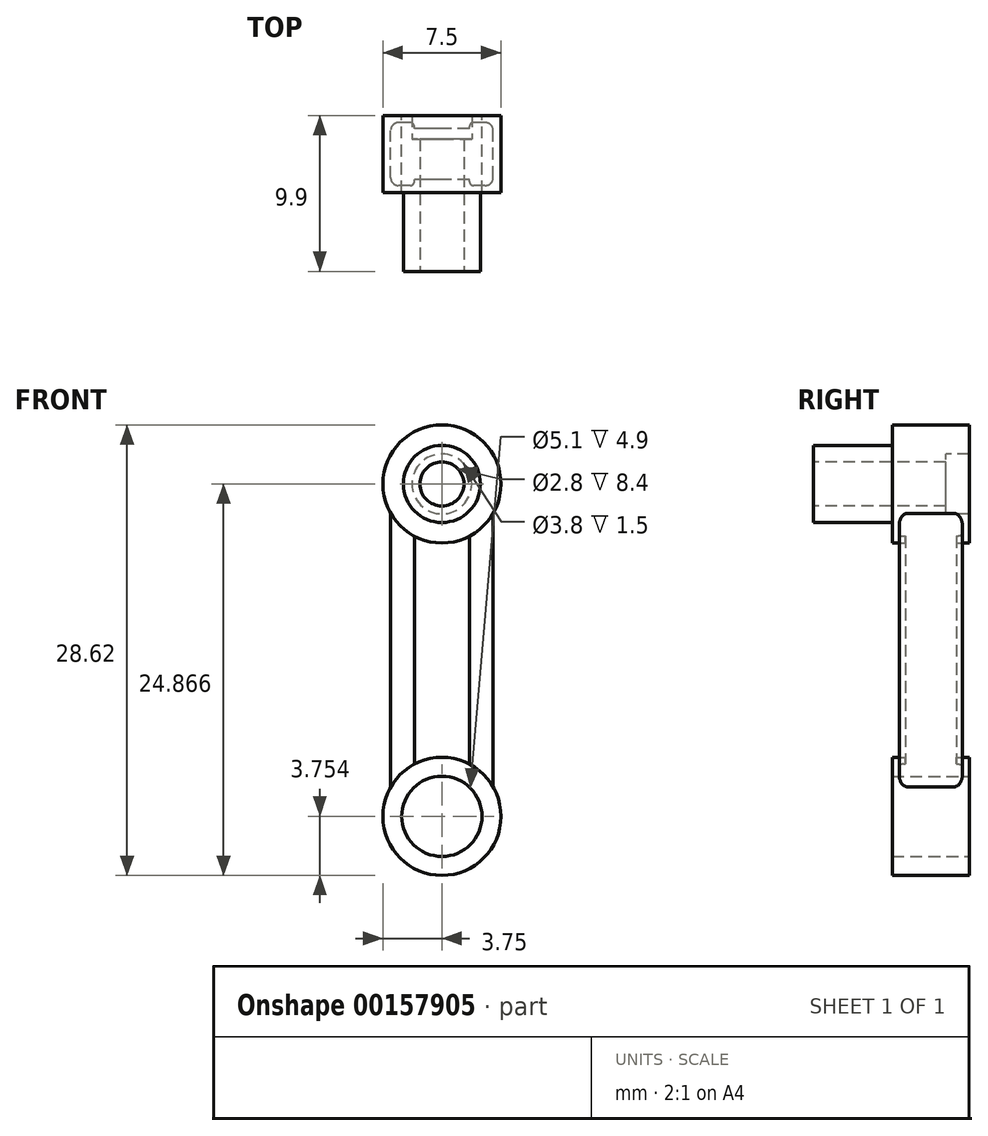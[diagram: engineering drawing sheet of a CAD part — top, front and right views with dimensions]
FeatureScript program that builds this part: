
annotation { "Feature Type Name" : "Feature", "Feature Type Description" : "" }
export const myFeature = defineFeature(function(context is Context, id is Id, definition is map)
    precondition{}
    {
        {
            var Q0;
            Q0=qCreatedBy(makeId("Front.planeOp"),FACE);
            var sketch = newSketch(context, id + "F0", { "sketchPlane" : qUnion([Q0])});
            skCircle(sketch, "E0", {"center": v(0, 10.56) * mm, "radius": 2.45 * mm});
            skCircle(sketch, "E1", {"center": v(0, -10.56) * mm, "radius": 2.55 * mm});
            skCircle(sketch, "E2", {"center": v(0, -10.56) * mm, "radius": 3.75 * mm});
            skCircle(sketch, "E3", {"center": v(0, 10.56) * mm, "radius": 3.75 * mm});
            skSolve(sketch);
        }
        {
            var Q0;
            Q0 = qSketchRegion(id + "F0", true);
            var Q1;
            Q1=makeQuery(id+"F0.imprint","IMPRINT",FACE,{"disambiguationData":[TD([[makeQuery(id+"F0.imprint","IMPRINT",EDGE,{"derivedFrom":sQuery(id+"F0.wireOp",EDGE,"E0")}),1.0]])]});
            extrude(context, id + "F1", {"entities" : qUnion([Q0, Q1]), "depth" : 4.9 * mm});
        }
        {
            var Q0;
            Q0=qCreatedBy(makeId("Top.planeOp"),FACE);
            var sketch = newSketch(context, id + "F2", { "sketchPlane" : qUnion([Q0])});
            skLineSegment(sketch, "E4.bottom", {"start": v(-2.75, -0.45) * mm, "end": v(-2, -0.45) * mm});
            skLineSegment(sketch, "E4.top", {"start": v(-2.75, -4.45) * mm, "end": v(-2, -4.45) * mm});
            skLineSegment(sketch, "E4.left", {"start": v(-3.25, -0.95) * mm, "end": v(-3.25, -3.95) * mm});
            skLineSegment(sketch, "E4.right", {"start": v(3.25, -0.95) * mm, "end": v(3.25, -3.95) * mm});
            skLineSegment(sketch, "E5.bottom", {"start": v(-1.75, -0.82) * mm, "end": v(1.75, -0.82) * mm});
            skLineSegment(sketch, "E5.top", {"start": v(-1.75, -4.08) * mm, "end": v(1.75, -4.08) * mm});
            skLineSegment(sketch, "E6", {"start": v(1.75, -4.08) * mm, "end": v(1.75, -4.2) * mm});
            skLineSegment(sketch, "E7", {"start": v(-1.75, -4.08) * mm, "end": v(-1.75, -4.2) * mm});
            skLineSegment(sketch, "E8", {"start": v(-1.75, -0.82) * mm, "end": v(-1.75, -0.7) * mm});
            skLineSegment(sketch, "E9", {"start": v(1.75, -0.82) * mm, "end": v(1.75, -0.7) * mm});
            skLineSegment(sketch, "E10.trimOffspring", {"start": v(2, -0.45) * mm, "end": v(2.75, -0.45) * mm});
            skLineSegment(sketch, "E11.trimOffspring", {"start": v(2, -4.45) * mm, "end": v(2.75, -4.45) * mm});
            skPoint(sketch, "E12.visualSharp", {"position": v(-1.75, -0.45) * mm});
            skArc(sketch, "E12.filletArc", {"start": v(-1.75, -0.7) * mm, "mid": v(-1.82, -0.52) * mm, "end": v(-2, -0.45) * mm});
            skPoint(sketch, "E13.visualSharp", {"position": v(1.75, -0.45) * mm});
            skArc(sketch, "E13.filletArc", {"start": v(2, -0.45) * mm, "mid": v(1.82, -0.52) * mm, "end": v(1.75, -0.7) * mm});
            skPoint(sketch, "E14.visualSharp", {"position": v(1.75, -4.45) * mm});
            skArc(sketch, "E14.filletArc", {"start": v(1.75, -4.2) * mm, "mid": v(1.82, -4.38) * mm, "end": v(2, -4.45) * mm});
            skPoint(sketch, "E15.visualSharp", {"position": v(-1.75, -4.45) * mm});
            skArc(sketch, "E15.filletArc", {"start": v(-2, -4.45) * mm, "mid": v(-1.82, -4.38) * mm, "end": v(-1.75, -4.2) * mm});
            skPoint(sketch, "E16.visualSharp", {"position": v(3.25, -4.45) * mm});
            skArc(sketch, "E16.filletArc", {"start": v(2.75, -4.45) * mm, "mid": v(3.1, -4.3) * mm, "end": v(3.25, -3.95) * mm});
            skPoint(sketch, "E17.visualSharp", {"position": v(3.25, -0.45) * mm});
            skArc(sketch, "E17.filletArc", {"start": v(3.25, -0.95) * mm, "mid": v(3.1, -0.6) * mm, "end": v(2.75, -0.45) * mm});
            skPoint(sketch, "E18.visualSharp", {"position": v(-3.25, -0.45) * mm});
            skArc(sketch, "E18.filletArc", {"start": v(-2.75, -0.45) * mm, "mid": v(-3.1, -0.6) * mm, "end": v(-3.25, -0.95) * mm});
            skPoint(sketch, "E19.visualSharp", {"position": v(-3.25, -4.45) * mm});
            skArc(sketch, "E19.filletArc", {"start": v(-3.25, -3.95) * mm, "mid": v(-3.1, -4.3) * mm, "end": v(-2.75, -4.45) * mm});
            skSolve(sketch);
        }
        {
            var Q0;
            Q0 = qSketchRegion(id + "F2", true);
            var Q1;
            Q1=makeQuery(id+"F1.opExtrude","SWEPT_FACE",FACE,{"disambiguationData":[OSD([sQuery(id+"F0.wireOp",EDGE,"E3")])]});
            extrude(context, id + "F3", {"entities" : qUnion([Q0]), "operationType" : NewBodyOperationType.ADD, "endBound" : BoundingType.UP_TO_SURFACE, "endBoundEntityFace" : qUnion([Q1]), "depth" : 25 * mm});
        }
        {
            var Q0;
            Q0=makeQuery(id+"F3.opExtrude","CAP_FACE",FACE,{"disambiguationData":[OSD([sQuery(id+"F2.wireOp",EDGE,"E4.bottom"),sQuery(id+"F2.wireOp",EDGE,"E4.top"),sQuery(id+"F2.wireOp",EDGE,"E4.left"),sQuery(id+"F2.wireOp",EDGE,"E4.right"),sQuery(id+"F2.wireOp",EDGE,"E5.bottom"),sQuery(id+"F2.wireOp",EDGE,"E5.top"),sQuery(id+"F2.wireOp",EDGE,"E6"),sQuery(id+"F2.wireOp",EDGE,"E7"),sQuery(id+"F2.wireOp",EDGE,"E8"),sQuery(id+"F2.wireOp",EDGE,"E9"),sQuery(id+"F2.wireOp",EDGE,"E10.trimOffspring"),sQuery(id+"F2.wireOp",EDGE,"E11.trimOffspring"),sQuery(id+"F2.wireOp",EDGE,"E12.filletArc"),sQuery(id+"F2.wireOp",EDGE,"E13.filletArc"),sQuery(id+"F2.wireOp",EDGE,"E14.filletArc"),sQuery(id+"F2.wireOp",EDGE,"E15.filletArc"),sQuery(id+"F2.wireOp",EDGE,"E16.filletArc"),sQuery(id+"F2.wireOp",EDGE,"E17.filletArc"),sQuery(id+"F2.wireOp",EDGE,"E18.filletArc"),sQuery(id+"F2.wireOp",EDGE,"E19.filletArc")])],"isStart":true});
            var Q1;
            Q1=makeQuery(id+"F1.opExtrude","SWEPT_FACE",FACE,{"disambiguationData":[OSD([sQuery(id+"F0.wireOp",EDGE,"E2")])]});
            extrude(context, id + "F4", {"entities" : qUnion([Q0]), "operationType" : NewBodyOperationType.ADD, "endBound" : BoundingType.UP_TO_SURFACE, "endBoundEntityFace" : qUnion([Q1]), "depth" : 25 * mm});
        }
        {
            var Q0;
            Q0=makeQuery(id+"F1.opExtrude","CAP_FACE",FACE,{"disambiguationData":[OSD([sQuery(id+"F0.wireOp",EDGE,"E3")])],"isStart":true});
            var sketch = newSketch(context, id + "F5", { "sketchPlane" : qUnion([Q0])});
            skCircle(sketch, "E20", {"center": v(0, 10.56) * mm, "radius": 0.6 * mm});
            skSolve(sketch);
        }
        {
            var Q0;
            Q0=makeQuery(id+"F1.opExtrude","CAP_FACE",FACE,{"disambiguationData":[OSD([sQuery(id+"F0.wireOp",EDGE,"E3")])],"isStart":false});
            var sketch = newSketch(context, id + "F6", { "sketchPlane" : qUnion([Q0])});
            skCircle(sketch, "E21", {"center": v(0, 10.56) * mm, "radius": 2.45 * mm});
            skSolve(sketch);
        }
        {
            var Q0;
            Q0 = qSketchRegion(id + "F6", true);
            extrude(context, id + "F7", {"entities" : qUnion([Q0]), "operationType" : NewBodyOperationType.ADD, "depth" : 5 * mm});
        }
        {
            var Q0;
            Q0=sQuery(id+"F5.wireOp",VERTEX,"E20.center");
            var Q1;
            Q1=makeQuery(id+"F1.opExtrude","SWEPT_BODY",BODY,{"disambiguationData":[OSD([sQuery(id+"F0.wireOp",EDGE,"E1"),sQuery(id+"F0.wireOp",EDGE,"E2")])]});
            hole(context, id + "F8", {"style" : HoleStyle.C_BORE, "endStyle" : HoleEndStyle.THROUGH, "holeDiameter" : 2.8 * mm, "cBoreDiameter" : 3.8 * mm, "cBoreDepth" : 1.5 * mm, "locations" : qUnion([Q0]), "scope" : qUnion([Q1]), "isTappedThrough" : true, "startStyle" : HoleStartStyle.SKETCH});
        }
    });
